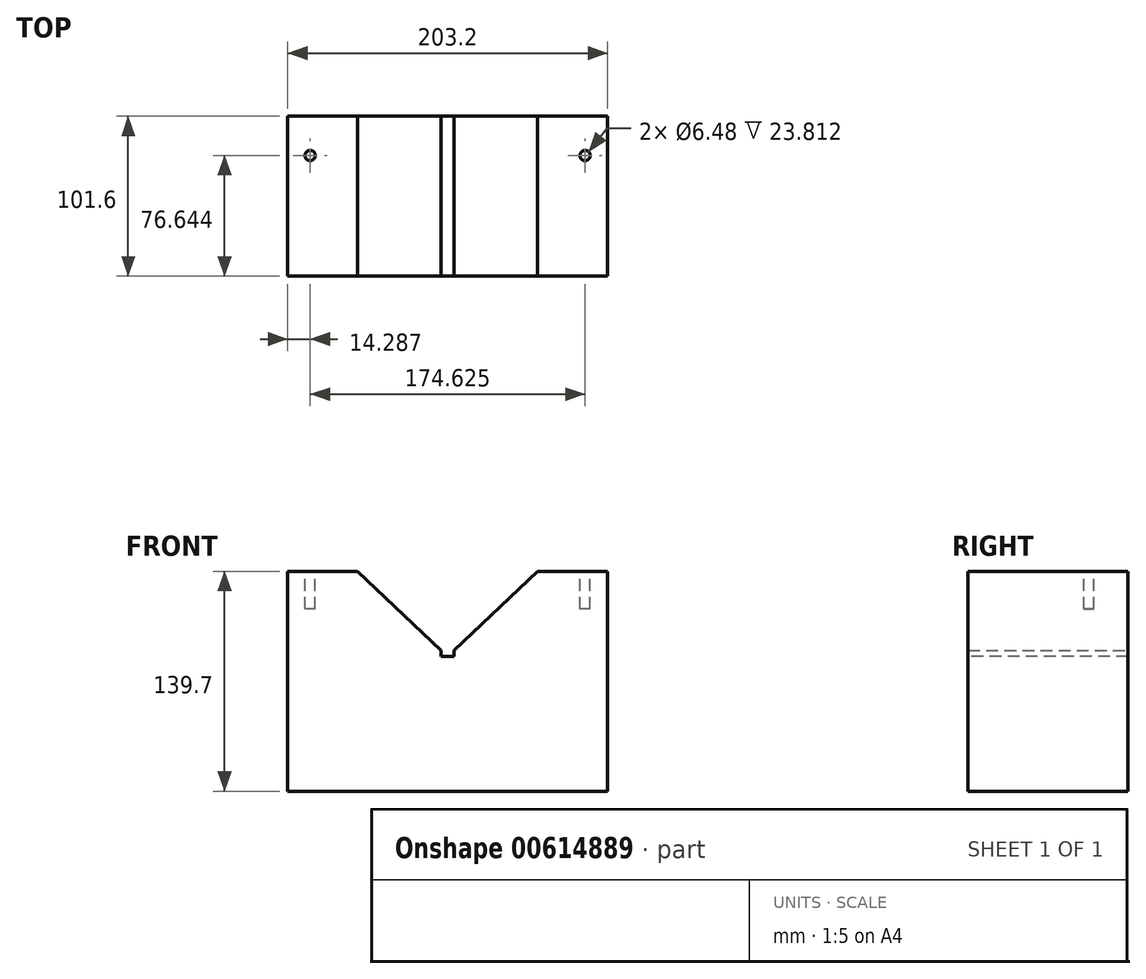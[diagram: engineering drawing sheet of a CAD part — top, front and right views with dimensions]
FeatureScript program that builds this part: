
annotation { "Feature Type Name" : "Feature", "Feature Type Description" : "" }
export const myFeature = defineFeature(function(context is Context, id is Id, definition is map)
    precondition{}
    {
        {
            var Q0;
            Q0=qCreatedBy(makeId("Front.planeOp"),FACE);
            var sketch = newSketch(context, id + "F0", { "sketchPlane" : qUnion([Q0])});
            skLineSegment(sketch, "E0", {"start": v(-101.6, 0) * mm, "end": v(101.6, 0) * mm});
            skLineSegment(sketch, "E1", {"start": v(-101.6, 0) * mm, "end": v(-101.6, 139.7) * mm});
            skLineSegment(sketch, "E2", {"start": v(-101.6, 139.7) * mm, "end": v(101.6, 139.7) * mm});
            skLineSegment(sketch, "E3", {"start": v(101.6, 139.7) * mm, "end": v(101.6, 0) * mm});
            skSolve(sketch);
        }
        {
            var Q0;
            Q0 = qSketchRegion(id + "F0", true);
            extrude(context, id + "F1", {"entities" : qUnion([Q0]), "endBound" : BoundingType.SYMMETRIC, "depth" : 101.6 * mm, "offsetDistance" : 25.4 * mm});
        }
        {
            var Q0;
            Q0=makeQuery(id+"F1.opExtrude","CAP_FACE",FACE,{"disambiguationData":[OSD([sQuery(id+"F0.wireOp",EDGE,"E0"),sQuery(id+"F0.wireOp",EDGE,"E1"),sQuery(id+"F0.wireOp",EDGE,"E2"),sQuery(id+"F0.wireOp",EDGE,"E3")])],"isStart":false});
            var sketch = newSketch(context, id + "F2", { "sketchPlane" : qUnion([Q0])});
            skLineSegment(sketch, "E4", {"start": v(0, 139.7) * mm, "end": v(0, 85.73) * mm});
            skPoint(sketch, "E4.endSnap0", {"position": v(0, 139.7) * mm});
            skLineSegment(sketch, "E5", {"start": v(0, 85.73) * mm, "end": v(-57.15, 139.7) * mm});
            skLineSegment(sketch, "E6", {"start": v(0, 85.73) * mm, "end": v(57.15, 139.7) * mm});
            skLineSegment(sketch, "E7", {"start": v(-57.15, 139.7) * mm, "end": v(57.15, 139.7) * mm});
            skSolve(sketch);
        }
        {
            var Q0;
            Q0 = qSketchRegion(id + "F2", true);
            extrude(context, id + "F3", {"entities" : qUnion([Q0]), "operationType" : NewBodyOperationType.REMOVE, "endBound" : BoundingType.THROUGH_ALL, "oppositeDirection" : true, "depth" : 25.4 * mm, "offsetDistance" : 25.4 * mm});
        }
        {
            var Q0;
            Q0=makeQuery(id+"F1.opExtrude","CAP_FACE",FACE,{"disambiguationData":[OSD([sQuery(id+"F0.wireOp",EDGE,"E0"),sQuery(id+"F0.wireOp",EDGE,"E1"),sQuery(id+"F0.wireOp",EDGE,"E2"),sQuery(id+"F0.wireOp",EDGE,"E3")])],"isStart":false});
            var sketch = newSketch(context, id + "F4", { "sketchPlane" : qUnion([Q0])});
            skLineSegment(sketch, "E8", {"start": v(-4.06, 85.73) * mm, "end": v(4.06, 85.73) * mm});
            skLineSegment(sketch, "E9", {"start": v(-4.06, 85.73) * mm, "end": v(-4.06, 90.04) * mm});
            skLineSegment(sketch, "E10", {"start": v(4.06, 85.73) * mm, "end": v(4.06, 90.04) * mm});
            skLineSegment(sketch, "E11", {"start": v(-4.06, 90.04) * mm, "end": v(4.06, 90.04) * mm});
            skLineSegment(sketch, "E12", {"start": v(-57.15, 139.7) * mm, "end": v(57.15, 139.7) * mm});
            skLineSegment(sketch, "E13", {"start": v(0, 139.7) * mm, "end": v(0, 90.04) * mm});
            skSolve(sketch);
        }
        {
            var Q0;
            Q0 = qSketchRegion(id + "F4", true);
            extrude(context, id + "F5", {"entities" : qUnion([Q0]), "operationType" : NewBodyOperationType.REMOVE, "endBound" : BoundingType.THROUGH_ALL, "oppositeDirection" : true, "depth" : 25.4 * mm, "offsetDistance" : 25.4 * mm});
        }
        {
            var Q0;
            {var subQ1=sQuery(id+"F0.wireOp",EDGE,"E2");var subQ2=sQuery(id+"F0.wireOp",EDGE,"E1");Q0=makeQuery(id+"F3.boolean.opBoolean","SPLIT",FACE,{"disambiguationData":[TD([makeQuery(id+"F1.opExtrude","SWEPT_FACE",FACE,{"disambiguationData":[OSD([subQ2])]})])],"derivedFrom":makeQuery(id+"F1.opExtrude","SWEPT_FACE",FACE,{"disambiguationData":[OSD([subQ1])]})});}
            var sketch = newSketch(context, id + "F6", { "sketchPlane" : qUnion([Q0])});
            skCircle(sketch, "E14", {"center": v(-87.31, 25.84) * mm, "radius": 3.24 * mm});
            skLineSegment(sketch, "E15", {"start": v(0, 50.8) * mm, "end": v(0, -50.8) * mm});
            skCircle(sketch, "E16.MirrorC", {"center": v(87.31, 25.84) * mm, "radius": 3.24 * mm});
            skSolve(sketch);
        }
        {
            var Q0;
            Q0 = qSketchRegion(id + "F6", true);
            extrude(context, id + "F7", {"entities" : qUnion([Q0]), "operationType" : NewBodyOperationType.REMOVE, "oppositeDirection" : true, "depth" : 23.8 * mm, "offsetDistance" : 25.4 * mm});
        }
    });
